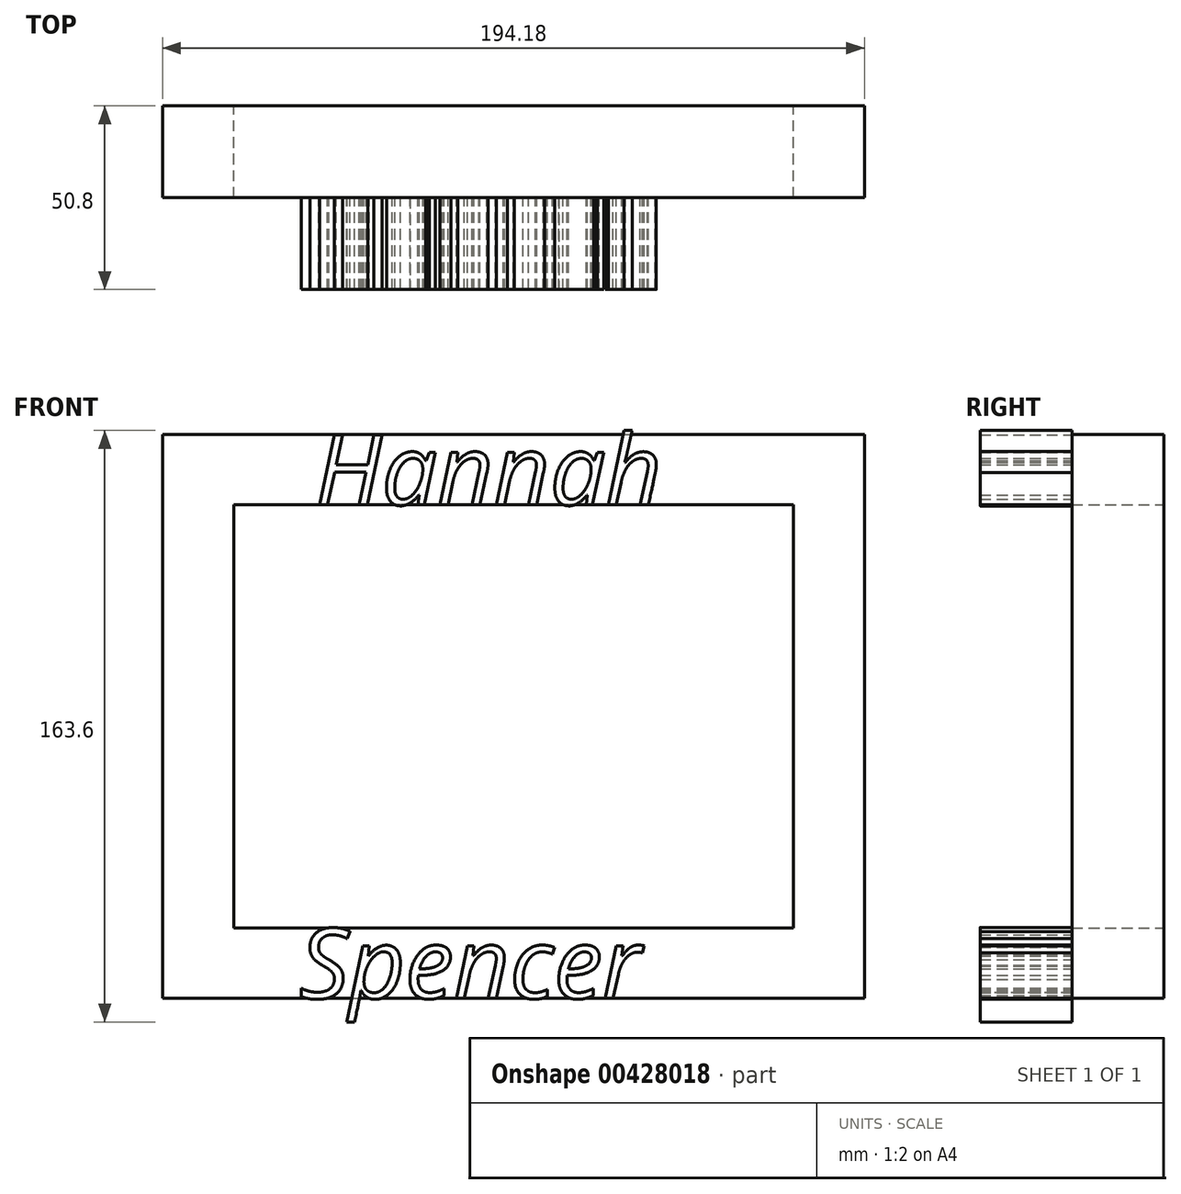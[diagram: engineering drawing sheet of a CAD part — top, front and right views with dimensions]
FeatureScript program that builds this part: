
annotation { "Feature Type Name" : "Feature", "Feature Type Description" : "" }
export const myFeature = defineFeature(function(context is Context, id is Id, definition is map)
    precondition{}
    {
        {
            var Q0;
            Q0=qCreatedBy(makeId("Front.planeOp"),FACE);
            var sketch = newSketch(context, id + "F0", { "sketchPlane" : qUnion([Q0])});
            skLineSegment(sketch, "E0.bottom", {"start": v(-97.09, 96.88) * mm, "end": v(97.09, 96.88) * mm});
            skLineSegment(sketch, "E0.top", {"start": v(-97.09, -59.13) * mm, "end": v(97.09, -59.13) * mm});
            skLineSegment(sketch, "E0.left", {"start": v(-97.09, 96.88) * mm, "end": v(-97.09, -59.13) * mm});
            skLineSegment(sketch, "E0.right", {"start": v(97.09, 96.88) * mm, "end": v(97.09, -59.13) * mm});
            skPoint(sketch, "E0.middle", {"position": v(0, 18.88) * mm});
            skLineSegment(sketch, "E1.bottom", {"start": v(77.38, 77.38) * mm, "end": v(-77.38, 77.38) * mm});
            skLineSegment(sketch, "E1.top", {"start": v(77.38, -39.62) * mm, "end": v(-77.38, -39.62) * mm});
            skLineSegment(sketch, "E1.left", {"start": v(77.38, 77.38) * mm, "end": v(77.38, -39.62) * mm});
            skLineSegment(sketch, "E1.right", {"start": v(-77.38, 77.38) * mm, "end": v(-77.38, -39.62) * mm});
            skSolve(sketch);
        }
        {
            var Q0;
            Q0 = qSketchRegion(id + "F0", true);
            extrude(context, id + "F1", {"entities" : qUnion([Q0]), "depth" : 25.4 * mm});
        }
        {
            var Q0;
            Q0=makeQuery(id+"F1.opExtrude","CAP_FACE",FACE,{"disambiguationData":[OSD([sQuery(id+"F0.wireOp",EDGE,"E0.bottom"),sQuery(id+"F0.wireOp",EDGE,"E0.top"),sQuery(id+"F0.wireOp",EDGE,"E0.left"),sQuery(id+"F0.wireOp",EDGE,"E0.right"),sQuery(id+"F0.wireOp",EDGE,"E1.bottom"),sQuery(id+"F0.wireOp",EDGE,"E1.top"),sQuery(id+"F0.wireOp",EDGE,"E1.left"),sQuery(id+"F0.wireOp",EDGE,"E1.right")])],"isStart":false});
            var sketch = newSketch(context, id + "F2", { "sketchPlane" : qUnion([Q0])});
            skText(sketch, "E2", { "text": " Hannah", "fontName": "OpenSans-Italic.ttf"});
            const initialGuessF2  = {"E2": [-0.06184, 0.07738, 1, 0, 0.0195]};
            skSetInitialGuess(sketch, initialGuessF2);
            skSolve(sketch);
        }
        {
            var Q0;
            Q0 = qSketchRegion(id + "F2", true);
            extrude(context, id + "F3", {"entities" : qUnion([Q0]), "operationType" : NewBodyOperationType.ADD, "depth" : 25.4 * mm});
        }
        {
            var Q0;
            {var subQ7=sQuery(id+"F0.wireOp",EDGE,"E0.left");var subQ10=sQuery(id+"F0.wireOp",EDGE,"E1.right");var subQ14=sQuery(id+"F0.wireOp",EDGE,"E1.left");var subQ16=sQuery(id+"F0.wireOp",EDGE,"E1.top");var subQ27=sQuery(id+"F0.wireOp",EDGE,"E1.bottom");var subQ28=sQuery(id+"F0.wireOp",EDGE,"E0.bottom");var subQ30=sQuery(id+"F0.wireOp",EDGE,"E0.right");var subQ32=sQuery(id+"F0.wireOp",EDGE,"E0.top");Q0=makeQuery(id+"F3.boolean.opBoolean","SPLIT",FACE,{"disambiguationData":[TD([makeQuery(id+"F1.opExtrude","SWEPT_FACE",FACE,{"disambiguationData":[OSD([subQ28])]})])],"derivedFrom":makeQuery(id+"F1.opExtrude","CAP_FACE",FACE,{"disambiguationData":[OSD([subQ28,subQ32,subQ7,subQ30,subQ27,subQ16,subQ14,subQ10])],"isStart":false})});}
            var sketch = newSketch(context, id + "F4", { "sketchPlane" : qUnion([Q0])});
            skText(sketch, "E3", { "text": " Spencer", "fontName": "OpenSans-Italic.ttf"});
            const initialGuessF4  = {"E3": [-0.06623, -0.05913, 1, 0, 0.0195]};
            skSetInitialGuess(sketch, initialGuessF4);
            skSolve(sketch);
        }
        {
            var Q0;
            Q0 = qSketchRegion(id + "F4", true);
            extrude(context, id + "F5", {"entities" : qUnion([Q0]), "operationType" : NewBodyOperationType.ADD, "depth" : 25.4 * mm});
        }
    });
